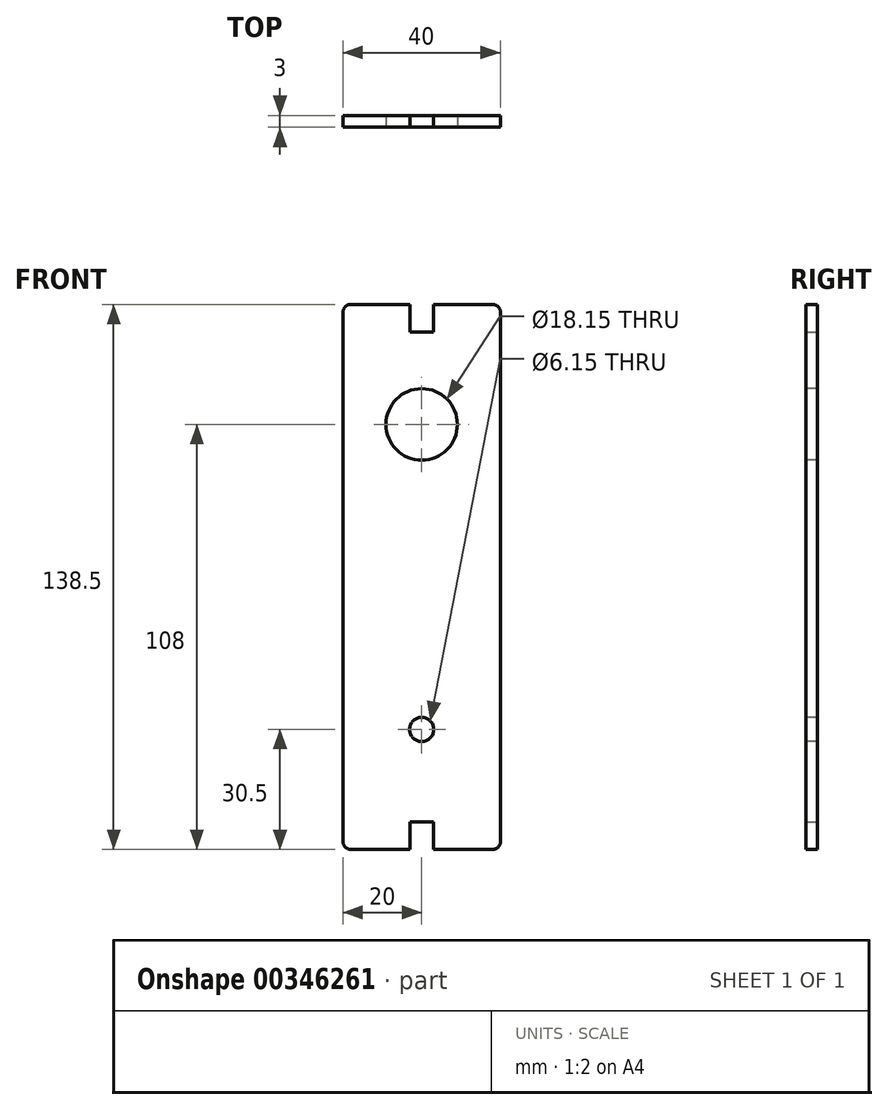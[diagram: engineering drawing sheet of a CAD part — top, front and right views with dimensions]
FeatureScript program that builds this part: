
annotation { "Feature Type Name" : "Feature", "Feature Type Description" : "" }
export const myFeature = defineFeature(function(context is Context, id is Id, definition is map)
    precondition{}
    {
        {
            var Q0;
            Q0=qCreatedBy(makeId("Front.planeOp"),FACE);
            var sketch = newSketch(context, id + "F0", { "sketchPlane" : qUnion([Q0])});
            skLineSegment(sketch, "E0", {"start": v(0, 0) * mm, "end": v(-3, 0) * mm});
            skLineSegment(sketch, "E1", {"start": v(-3, 0) * mm, "end": v(-3, 7) * mm});
            skLineSegment(sketch, "E2", {"start": v(-3, 7) * mm, "end": v(-20, 7) * mm});
            skLineSegment(sketch, "E3", {"start": v(-20, 7) * mm, "end": v(-20, -131.5) * mm});
            skLineSegment(sketch, "E4", {"start": v(-20, -131.5) * mm, "end": v(-3, -131.5) * mm});
            skLineSegment(sketch, "E5", {"start": v(-3, -131.5) * mm, "end": v(-3, -124.5) * mm});
            skLineSegment(sketch, "E6", {"start": v(-3, -124.5) * mm, "end": v(0, -124.5) * mm});
            skLineSegment(sketch, "E7", {"start": v(0, -124.5) * mm, "end": v(0, 0) * mm});
            skSolve(sketch);
        }
        {
            var Q0;
            Q0=makeQuery(id+"F0.imprint","IMPRINT",FACE,{"disambiguationData":[TD([[makeQuery(id+"F0.imprint","IMPRINT",EDGE,{"derivedFrom":sQuery(id+"F0.wireOp",EDGE,"E0")}),1.0]])]});
            extrude(context, id + "F1", {"entities" : qUnion([Q0]), "depth" : 3 * mm});
        }
        {
            var Q0;
            Q0=makeQuery(id+"F1.opExtrude","SWEPT_BODY",BODY,{"disambiguationData":[OSD([sQuery(id+"F0.wireOp",EDGE,"E0"),sQuery(id+"F0.wireOp",EDGE,"E1"),sQuery(id+"F0.wireOp",EDGE,"E2"),sQuery(id+"F0.wireOp",EDGE,"E3"),sQuery(id+"F0.wireOp",EDGE,"E4"),sQuery(id+"F0.wireOp",EDGE,"E5"),sQuery(id+"F0.wireOp",EDGE,"E6"),sQuery(id+"F0.wireOp",EDGE,"E7")])]});
            var Q1;
            Q1=qCreatedBy(makeId("Right.planeOp"),FACE);
            mirror(context, id + "F2", {"operationType" : NewBodyOperationType.ADD, "entities" : qUnion([Q0]), "mirrorPlane" : qUnion([Q1])});
        }
        {
            var Q0;
            {var subQ0=makeQuery(id+"F1.opExtrude","CAP_FACE",FACE,{"disambiguationData":[OSD([sQuery(id+"F0.wireOp",EDGE,"E0"),sQuery(id+"F0.wireOp",EDGE,"E1"),sQuery(id+"F0.wireOp",EDGE,"E2"),sQuery(id+"F0.wireOp",EDGE,"E3"),sQuery(id+"F0.wireOp",EDGE,"E4"),sQuery(id+"F0.wireOp",EDGE,"E5"),sQuery(id+"F0.wireOp",EDGE,"E6"),sQuery(id+"F0.wireOp",EDGE,"E7")])],"isStart":false});Q0=makeQuery(id+"F2.boolean.opBoolean","MERGE",FACE,{"derivedFrom":[subQ0,makeQuery(id+"F2.opPattern","COPY",FACE,{"derivedFrom":subQ0,"instanceName":"1"})]});}
            var sketch = newSketch(context, id + "F3", { "sketchPlane" : qUnion([Q0])});
            skPoint(sketch, "E8", {"position": v(0, -23.5) * mm});
            skSolve(sketch);
        }
        {
            var Q0;
            Q0=sQuery(id+"F3.wireOp",VERTEX,"E8");
            var Q1;
            Q1=makeQuery(id+"F1.opExtrude","SWEPT_BODY",BODY,{"disambiguationData":[OSD([sQuery(id+"F0.wireOp",EDGE,"E0"),sQuery(id+"F0.wireOp",EDGE,"E1"),sQuery(id+"F0.wireOp",EDGE,"E2"),sQuery(id+"F0.wireOp",EDGE,"E3"),sQuery(id+"F0.wireOp",EDGE,"E4"),sQuery(id+"F0.wireOp",EDGE,"E5"),sQuery(id+"F0.wireOp",EDGE,"E6"),sQuery(id+"F0.wireOp",EDGE,"E7")])]});
            hole(context, id + "F4", {"style" : HoleStyle.SIMPLE, "endStyle" : HoleEndStyle.THROUGH, "holeDiameter" : 18.15 * mm, "isTappedThrough" : true, "tappedDepth" : 12 * mm, "tapClearance" : 3, "locations" : qUnion([Q0]), "scope" : qUnion([Q1])});
        }
        {
            var Q0;
            {var subQ0=makeQuery(id+"F1.opExtrude","CAP_FACE",FACE,{"disambiguationData":[OSD([sQuery(id+"F0.wireOp",EDGE,"E0"),sQuery(id+"F0.wireOp",EDGE,"E1"),sQuery(id+"F0.wireOp",EDGE,"E2"),sQuery(id+"F0.wireOp",EDGE,"E3"),sQuery(id+"F0.wireOp",EDGE,"E4"),sQuery(id+"F0.wireOp",EDGE,"E5"),sQuery(id+"F0.wireOp",EDGE,"E6"),sQuery(id+"F0.wireOp",EDGE,"E7")])],"isStart":false});Q0=makeQuery(id+"F2.boolean.opBoolean","MERGE",FACE,{"derivedFrom":[subQ0,makeQuery(id+"F2.opPattern","COPY",FACE,{"derivedFrom":subQ0,"instanceName":"1"})]});}
            var sketch = newSketch(context, id + "F5", { "sketchPlane" : qUnion([Q0])});
            skPoint(sketch, "E9", {"position": v(0, -101) * mm});
            skSolve(sketch);
        }
        {
            var Q0;
            Q0=sQuery(id+"F5.wireOp",VERTEX,"E9");
            var Q1;
            Q1=makeQuery(id+"F1.opExtrude","SWEPT_BODY",BODY,{"disambiguationData":[OSD([sQuery(id+"F0.wireOp",EDGE,"E0"),sQuery(id+"F0.wireOp",EDGE,"E1"),sQuery(id+"F0.wireOp",EDGE,"E2"),sQuery(id+"F0.wireOp",EDGE,"E3"),sQuery(id+"F0.wireOp",EDGE,"E4"),sQuery(id+"F0.wireOp",EDGE,"E5"),sQuery(id+"F0.wireOp",EDGE,"E6"),sQuery(id+"F0.wireOp",EDGE,"E7")])]});
            hole(context, id + "F6", {"style" : HoleStyle.SIMPLE, "endStyle" : HoleEndStyle.THROUGH, "holeDiameter" : 6.15 * mm, "isTappedThrough" : true, "tappedDepth" : 12 * mm, "tapClearance" : 3, "locations" : qUnion([Q0]), "scope" : qUnion([Q1])});
        }
        {
            var Q0;
            Q0=makeQuery(id+"F2.opPattern","COPY",EDGE,{"derivedFrom":makeQuery(id+"F1.opExtrude","SWEPT_EDGE",EDGE,{"disambiguationData":[OSD([sQuery(id+"F0.wireOp",EDGE,"E3"),sQuery(id+"F0.wireOp",EDGE,"E4")])]}),"instanceName":"1"});
            var Q1;
            Q1=makeQuery(id+"F1.opExtrude","SWEPT_EDGE",EDGE,{"disambiguationData":[OSD([sQuery(id+"F0.wireOp",EDGE,"E3"),sQuery(id+"F0.wireOp",EDGE,"E4")])]});
            var Q2;
            Q2=makeQuery(id+"F1.opExtrude","SWEPT_EDGE",EDGE,{"disambiguationData":[OSD([sQuery(id+"F0.wireOp",EDGE,"E2"),sQuery(id+"F0.wireOp",EDGE,"E3")])]});
            var Q3;
            Q3=makeQuery(id+"F2.opPattern","COPY",EDGE,{"derivedFrom":makeQuery(id+"F1.opExtrude","SWEPT_EDGE",EDGE,{"disambiguationData":[OSD([sQuery(id+"F0.wireOp",EDGE,"E2"),sQuery(id+"F0.wireOp",EDGE,"E3")])]}),"instanceName":"1"});
            fillet(context, id + "F7", {"entities" : qUnion([Q0, Q1, Q2, Q3]), "radius" : 2 * mm, "tangentPropagation" : true, "allowEdgeOverflow" : false});
        }
    });
